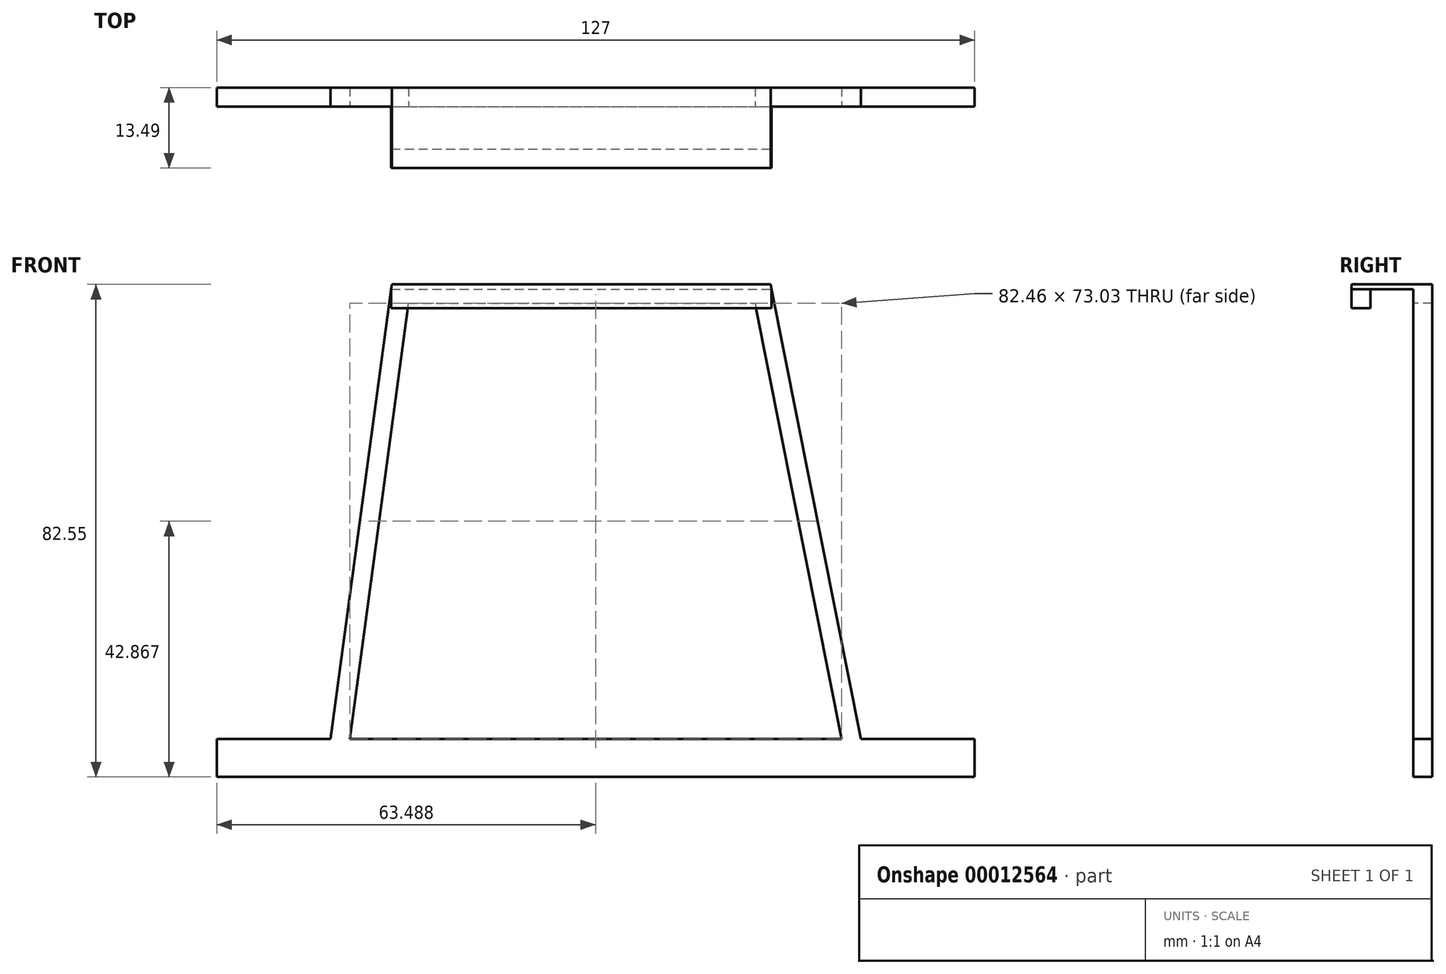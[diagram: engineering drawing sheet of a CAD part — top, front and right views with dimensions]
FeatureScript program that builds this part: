
annotation { "Feature Type Name" : "Feature", "Feature Type Description" : "" }
export const myFeature = defineFeature(function(context is Context, id is Id, definition is map)
    precondition{}
    {
        {
            var Q0;
            Q0=qCreatedBy(makeId("Front.planeOp"),FACE);
            var sketch = newSketch(context, id + "F0", { "sketchPlane" : qUnion([Q0])});
            skLineSegment(sketch, "E0.bottom", {"start": v(-42.96, 6.24) * mm, "end": v(-23.9, 6.24) * mm});
            skLineSegment(sketch, "E0.top", {"start": v(-42.96, -0.1) * mm, "end": v(84.04, -0.1) * mm});
            skLineSegment(sketch, "E0.left", {"start": v(-42.96, 6.24) * mm, "end": v(-42.96, -0.1) * mm});
            skLineSegment(sketch, "E0.right", {"start": v(84.04, 6.24) * mm, "end": v(84.04, -0.1) * mm});
            skLineSegment(sketch, "E1", {"start": v(-23.9, 6.24) * mm, "end": v(-13.63, 82.44) * mm});
            skLineSegment(sketch, "E2", {"start": v(-13.63, 82.44) * mm, "end": v(49.87, 82.44) * mm});
            skLineSegment(sketch, "E3", {"start": v(49.87, 82.44) * mm, "end": v(65, 6.24) * mm});
            skLineSegment(sketch, "E4.trimOffspring", {"start": v(65, 6.24) * mm, "end": v(84.04, 6.24) * mm});
            skSolve(sketch);
        }
        {
            var Q0;
            Q0 = qSketchRegion(id + "F0", true);
            extrude(context, id + "F1", {"entities" : qUnion([Q0]), "depth" : 3.17 * mm});
        }
        {
            var Q0;
            Q0=makeQuery(id+"F1.opExtrude","CAP_FACE",FACE,{"disambiguationData":[OSD([sQuery(id+"F0.wireOp",EDGE,"E0.bottom"),sQuery(id+"F0.wireOp",EDGE,"E0.top"),sQuery(id+"F0.wireOp",EDGE,"E0.left"),sQuery(id+"F0.wireOp",EDGE,"E0.right"),sQuery(id+"F0.wireOp",EDGE,"E1"),sQuery(id+"F0.wireOp",EDGE,"E2"),sQuery(id+"F0.wireOp",EDGE,"E3"),sQuery(id+"F0.wireOp",EDGE,"E4.trimOffspring")])],"isStart":false});
            var sketch = newSketch(context, id + "F2", { "sketchPlane" : qUnion([Q0])});
            skLineSegment(sketch, "E5.0", {"start": v(-23.9, 6.24) * mm, "end": v(-13.63, 82.44) * mm});
            skLineSegment(sketch, "E5.1", {"start": v(-13.63, 82.44) * mm, "end": v(49.87, 82.44) * mm});
            skLineSegment(sketch, "E5.2", {"start": v(49.87, 82.44) * mm, "end": v(65, 6.24) * mm});
            skLineSegment(sketch, "E6.0", {"start": v(47.27, 79.27) * mm, "end": v(61.76, 6.24) * mm});
            skLineSegment(sketch, "E6.1", {"start": v(-10.85, 79.27) * mm, "end": v(47.27, 79.27) * mm});
            skLineSegment(sketch, "E6.2", {"start": v(-20.7, 6.24) * mm, "end": v(-10.85, 79.27) * mm});
            skLineSegment(sketch, "E7", {"start": v(-20.7, 6.24) * mm, "end": v(61.76, 6.24) * mm});
            skSolve(sketch);
        }
        {
            var Q0;
            Q0=makeQuery(id+"F2.imprint","IMPRINT",FACE,{"disambiguationData":[TD([[makeQuery(id+"F2.imprint","IMPRINT",EDGE,{"derivedFrom":sQuery(id+"F2.wireOp",EDGE,"E6.0")}),-1.0]])]});
            extrude(context, id + "F3", {"entities" : qUnion([Q0]), "operationType" : NewBodyOperationType.REMOVE, "endBound" : BoundingType.THROUGH_ALL, "oppositeDirection" : true, "depth" : 25.4 * mm});
        }
        {
            var Q0;
            Q0=makeQuery(id+"F1.opExtrude","CAP_FACE",FACE,{"disambiguationData":[OSD([sQuery(id+"F0.wireOp",EDGE,"E0.bottom"),sQuery(id+"F0.wireOp",EDGE,"E0.top"),sQuery(id+"F0.wireOp",EDGE,"E0.left"),sQuery(id+"F0.wireOp",EDGE,"E0.right"),sQuery(id+"F0.wireOp",EDGE,"E1"),sQuery(id+"F0.wireOp",EDGE,"E2"),sQuery(id+"F0.wireOp",EDGE,"E3"),sQuery(id+"F0.wireOp",EDGE,"E4.trimOffspring")])],"isStart":false});
            var sketch = newSketch(context, id + "F4", { "sketchPlane" : qUnion([Q0])});
            skLineSegment(sketch, "E8.0", {"start": v(-13.63, 82.44) * mm, "end": v(49.87, 82.44) * mm});
            skLineSegment(sketch, "E9", {"start": v(-13.74, 81.65) * mm, "end": v(50.03, 81.65) * mm});
            skLineSegment(sketch, "E10", {"start": v(-13.74, 81.65) * mm, "end": v(-13.63, 82.44) * mm});
            skLineSegment(sketch, "E11", {"start": v(50.03, 81.65) * mm, "end": v(49.87, 82.44) * mm});
            skSolve(sketch);
        }
        {
            var Q0;
            Q0=makeQuery(id+"F4.imprint","IMPRINT",FACE,{"disambiguationData":[TD([[makeQuery(id+"F4.imprint","IMPRINT",EDGE,{"derivedFrom":sQuery(id+"F4.wireOp",EDGE,"E8.0")}),-1.0]])]});
            extrude(context, id + "F5", {"entities" : qUnion([Q0]), "operationType" : NewBodyOperationType.ADD, "depth" : 10.32 * mm});
        }
        {
            var Q0;
            Q0=makeQuery(id+"F5.opExtrude","SWEPT_FACE",FACE,{"disambiguationData":[OSD([sQuery(id+"F4.wireOp",EDGE,"E9")])]});
            var sketch = newSketch(context, id + "F6", { "sketchPlane" : qUnion([Q0])});
            skLineSegment(sketch, "E12.0", {"start": v(-13.74, 13.5) * mm, "end": v(50.03, 13.5) * mm});
            skLineSegment(sketch, "E13", {"start": v(-13.74, 10.32) * mm, "end": v(50.03, 10.32) * mm});
            skLineSegment(sketch, "E14", {"start": v(50.03, 10.32) * mm, "end": v(50.03, 13.5) * mm});
            skLineSegment(sketch, "E15", {"start": v(-13.74, 10.32) * mm, "end": v(-13.74, 13.5) * mm});
            skSolve(sketch);
        }
        {
            var Q0;
            Q0=makeQuery(id+"F6.imprint","IMPRINT",FACE,{"disambiguationData":[TD([[makeQuery(id+"F6.imprint","IMPRINT",EDGE,{"derivedFrom":sQuery(id+"F6.wireOp",EDGE,"E12.0")}),-1.0]])]});
            extrude(context, id + "F7", {"entities" : qUnion([Q0]), "operationType" : NewBodyOperationType.ADD, "depth" : 3.17 * mm});
        }
    });
